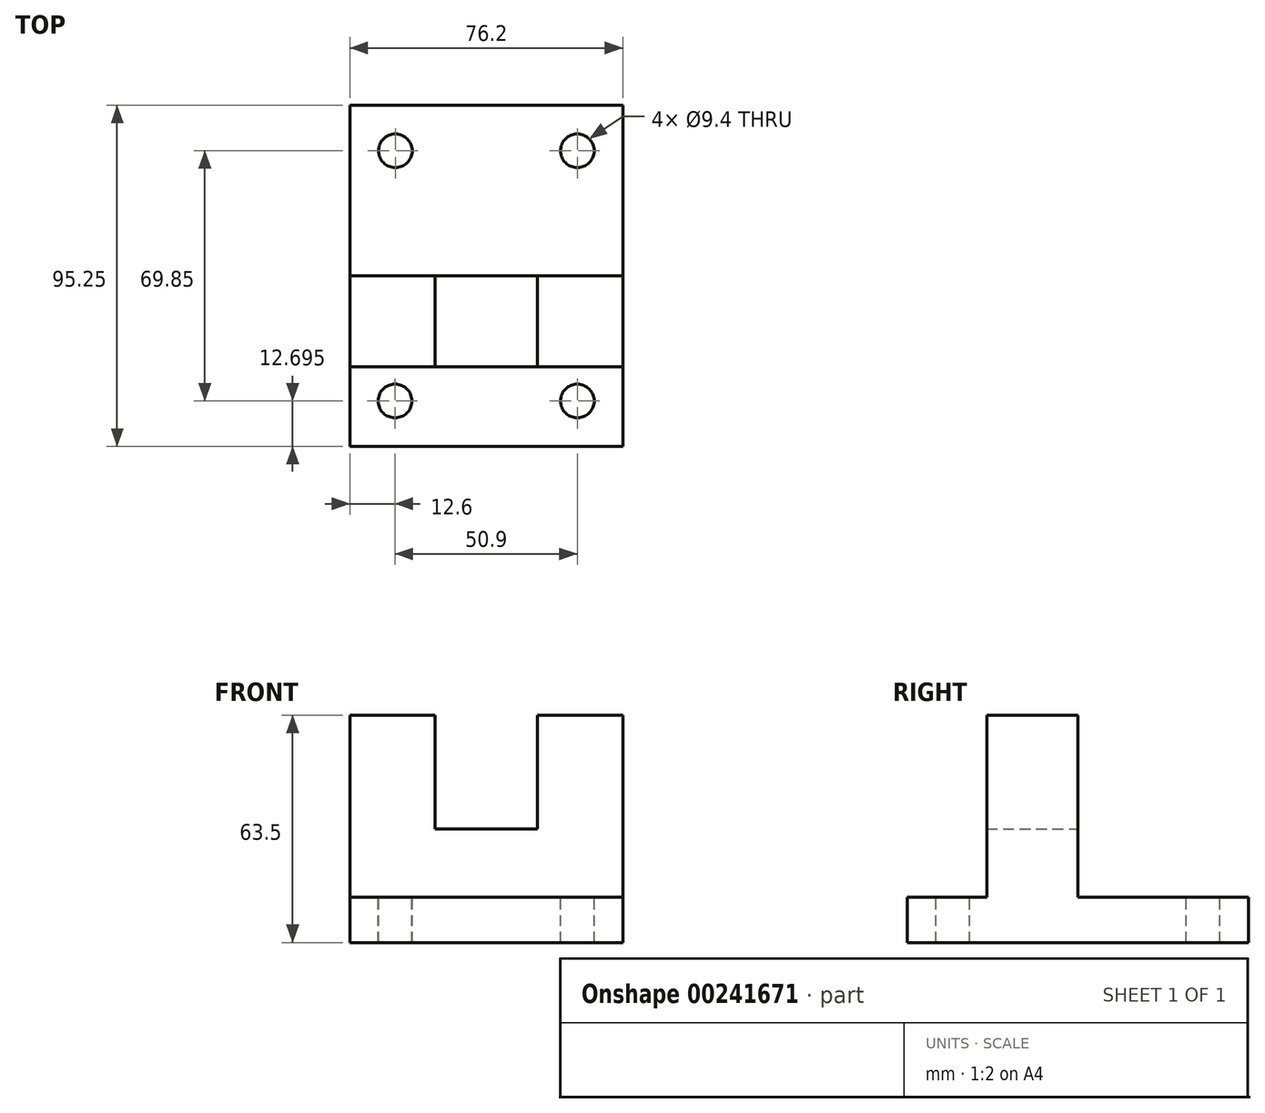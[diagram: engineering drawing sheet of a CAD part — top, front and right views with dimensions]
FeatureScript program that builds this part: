
annotation { "Feature Type Name" : "Feature", "Feature Type Description" : "" }
export const myFeature = defineFeature(function(context is Context, id is Id, definition is map)
    precondition{}
    {
        {
            var Q0;
            Q0=qCreatedBy(makeId("Front.planeOp"),FACE);
            var sketch = newSketch(context, id + "F0", { "sketchPlane" : qUnion([Q0])});
            skLineSegment(sketch, "E0.bottom", {"start": v(38.1, 31.75) * mm, "end": v(14.27, 31.75) * mm});
            skLineSegment(sketch, "E0.top", {"start": v(38.1, -31.75) * mm, "end": v(-38.1, -31.75) * mm});
            skLineSegment(sketch, "E0.left", {"start": v(38.1, 31.75) * mm, "end": v(38.1, -31.75) * mm});
            skLineSegment(sketch, "E0.right", {"start": v(-38.1, 31.75) * mm, "end": v(-38.1, -31.75) * mm});
            skPoint(sketch, "E0.middle", {"position": v(0, 0) * mm});
            skLineSegment(sketch, "E1", {"start": v(-14.27, 31.75) * mm, "end": v(-14.27, 0) * mm});
            skLineSegment(sketch, "E2", {"start": v(14.27, 0) * mm, "end": v(14.27, 31.75) * mm});
            skLineSegment(sketch, "E3", {"start": v(-14.27, 0) * mm, "end": v(14.27, 0) * mm});
            skLineSegment(sketch, "E4.trimOffspring", {"start": v(-14.27, 31.75) * mm, "end": v(-38.1, 31.75) * mm});
            skLineSegment(sketch, "E5", {"start": v(14.27, 0) * mm, "end": v(38.1, 0) * mm});
            skSolve(sketch);
        }
        {
            var Q0;
            Q0 = qSketchRegion(id + "F0", true);
            var Q1;
            Q1 = qConstructionFilter(qBodyType(qCreatedBy(id + "F0" ,EDGE), BodyType.WIRE), ConstructionObject.NO);
            extrude(context, id + "F1", {"entities" : qUnion([Q0]), "surfaceEntities" : qUnion([Q1]), "depth" : 25.4 * mm});
        }
        {
            var Q0;
            Q0=makeQuery(id+"F1.opExtrude","CAP_FACE",FACE,{"disambiguationData":[OSD([sQuery(id+"F0.wireOp",EDGE,"E0.bottom"),sQuery(id+"F0.wireOp",EDGE,"E0.top"),sQuery(id+"F0.wireOp",EDGE,"E0.left"),sQuery(id+"F0.wireOp",EDGE,"E0.right"),sQuery(id+"F0.wireOp",EDGE,"E1"),sQuery(id+"F0.wireOp",EDGE,"E2"),sQuery(id+"F0.wireOp",EDGE,"E3"),sQuery(id+"F0.wireOp",EDGE,"E4.trimOffspring")])],"isStart":true});
            var sketch = newSketch(context, id + "F2", { "sketchPlane" : qUnion([Q0])});
            skLineSegment(sketch, "E6.bottom", {"start": v(-38.1, -31.75) * mm, "end": v(38.1, -31.75) * mm});
            skLineSegment(sketch, "E6.top", {"start": v(-38.1, -19.05) * mm, "end": v(38.1, -19.05) * mm});
            skLineSegment(sketch, "E6.left", {"start": v(-38.1, -31.75) * mm, "end": v(-38.1, -19.05) * mm});
            skLineSegment(sketch, "E6.right", {"start": v(38.1, -31.75) * mm, "end": v(38.1, -19.05) * mm});
            skSolve(sketch);
        }
        {
            var Q0;
            Q0=makeQuery(id+"F2.imprint","IMPRINT",FACE,{"disambiguationData":[TD([[makeQuery(id+"F2.imprint","IMPRINT",EDGE,{"derivedFrom":sQuery(id+"F2.wireOp",EDGE,"E6.bottom")}),1.0]])]});
            extrude(context, id + "F3", {"entities" : qUnion([Q0]), "operationType" : NewBodyOperationType.ADD, "endBound" : BoundingType.SYMMETRIC, "oppositeDirection" : true, "depth" : 95.25 * mm});
        }
        {
            var Q0;
            {var subQ0=sQuery(id+"F2.wireOp",EDGE,"E6.right");var subQ1=sQuery(id+"F2.wireOp",EDGE,"E6.left");var subQ2=sQuery(id+"F2.wireOp",EDGE,"E6.top");Q0=makeQuery(id+"F3.boolean.opBoolean","SPLIT",FACE,{"disambiguationData":[TD([makeQuery(id+"F3.opExtrude","CAP_FACE",FACE,{"disambiguationData":[OSD([sQuery(id+"F2.wireOp",EDGE,"E6.bottom"),subQ2,subQ1,subQ0])],"isStart":false})])],"derivedFrom":makeQuery(id+"F3.opExtrude","SWEPT_FACE",FACE,{"disambiguationData":[OSD([subQ2])]})});}
            var sketch = newSketch(context, id + "F4", { "sketchPlane" : qUnion([Q0])});
            skPoint(sketch, "E7.centerSnap0", {"position": v(38.1, -36.51) * mm});
            skCircle(sketch, "E8", {"center": v(25.4, -34.93) * mm, "radius": 4.7 * mm});
            skCircle(sketch, "E9", {"center": v(-25.5, -34.93) * mm, "radius": 4.7 * mm});
            skSolve(sketch);
        }
        {
            var Q0;
            Q0=makeQuery(id+"F4.imprint","IMPRINT",FACE,{"disambiguationData":[TD([[makeQuery(id+"F4.imprint","IMPRINT",EDGE,{"derivedFrom":sQuery(id+"F4.wireOp",EDGE,"E9")}),1.0]])]});
            var Q1;
            Q1=makeQuery(id+"F4.imprint","IMPRINT",FACE,{"disambiguationData":[TD([[makeQuery(id+"F4.imprint","IMPRINT",EDGE,{"derivedFrom":sQuery(id+"F4.wireOp",EDGE,"E8")}),1.0]])]});
            extrude(context, id + "F5", {"entities" : qUnion([Q0, Q1]), "operationType" : NewBodyOperationType.REMOVE, "endBound" : BoundingType.THROUGH_ALL, "oppositeDirection" : true, "depth" : 29.2 * mm});
        }
        {
            var Q0;
            {var subQ2=sQuery(id+"F2.wireOp",EDGE,"E6.right");var subQ3=sQuery(id+"F2.wireOp",EDGE,"E6.left");var subQ4=sQuery(id+"F2.wireOp",EDGE,"E6.top");Q0=makeQuery(id+"F3.boolean.opBoolean","SPLIT",FACE,{"disambiguationData":[TD([makeQuery(id+"F3.opExtrude","CAP_FACE",FACE,{"disambiguationData":[OSD([sQuery(id+"F2.wireOp",EDGE,"E6.bottom"),subQ4,subQ3,subQ2])],"isStart":true})])],"derivedFrom":makeQuery(id+"F3.opExtrude","SWEPT_FACE",FACE,{"disambiguationData":[OSD([subQ4])]})});}
            var sketch = newSketch(context, id + "F6", { "sketchPlane" : qUnion([Q0])});
            skCircle(sketch, "E10", {"center": v(-25.4, 34.93) * mm, "radius": 4.7 * mm});
            skCircle(sketch, "E11", {"center": v(25.4, 34.93) * mm, "radius": 4.7 * mm});
            skSolve(sketch);
        }
        {
            var Q0;
            Q0=makeQuery(id+"F6.imprint","IMPRINT",FACE,{"disambiguationData":[TD([[makeQuery(id+"F6.imprint","IMPRINT",EDGE,{"derivedFrom":sQuery(id+"F6.wireOp",EDGE,"E10")}),1.0]])]});
            var Q1;
            Q1=makeQuery(id+"F6.imprint","IMPRINT",FACE,{"disambiguationData":[TD([[makeQuery(id+"F6.imprint","IMPRINT",EDGE,{"derivedFrom":sQuery(id+"F6.wireOp",EDGE,"E11")}),1.0]])]});
            extrude(context, id + "F7", {"entities" : qUnion([Q0, Q1]), "operationType" : NewBodyOperationType.REMOVE, "endBound" : BoundingType.SYMMETRIC, "oppositeDirection" : true, "depth" : 66.04 * mm});
        }
    });
